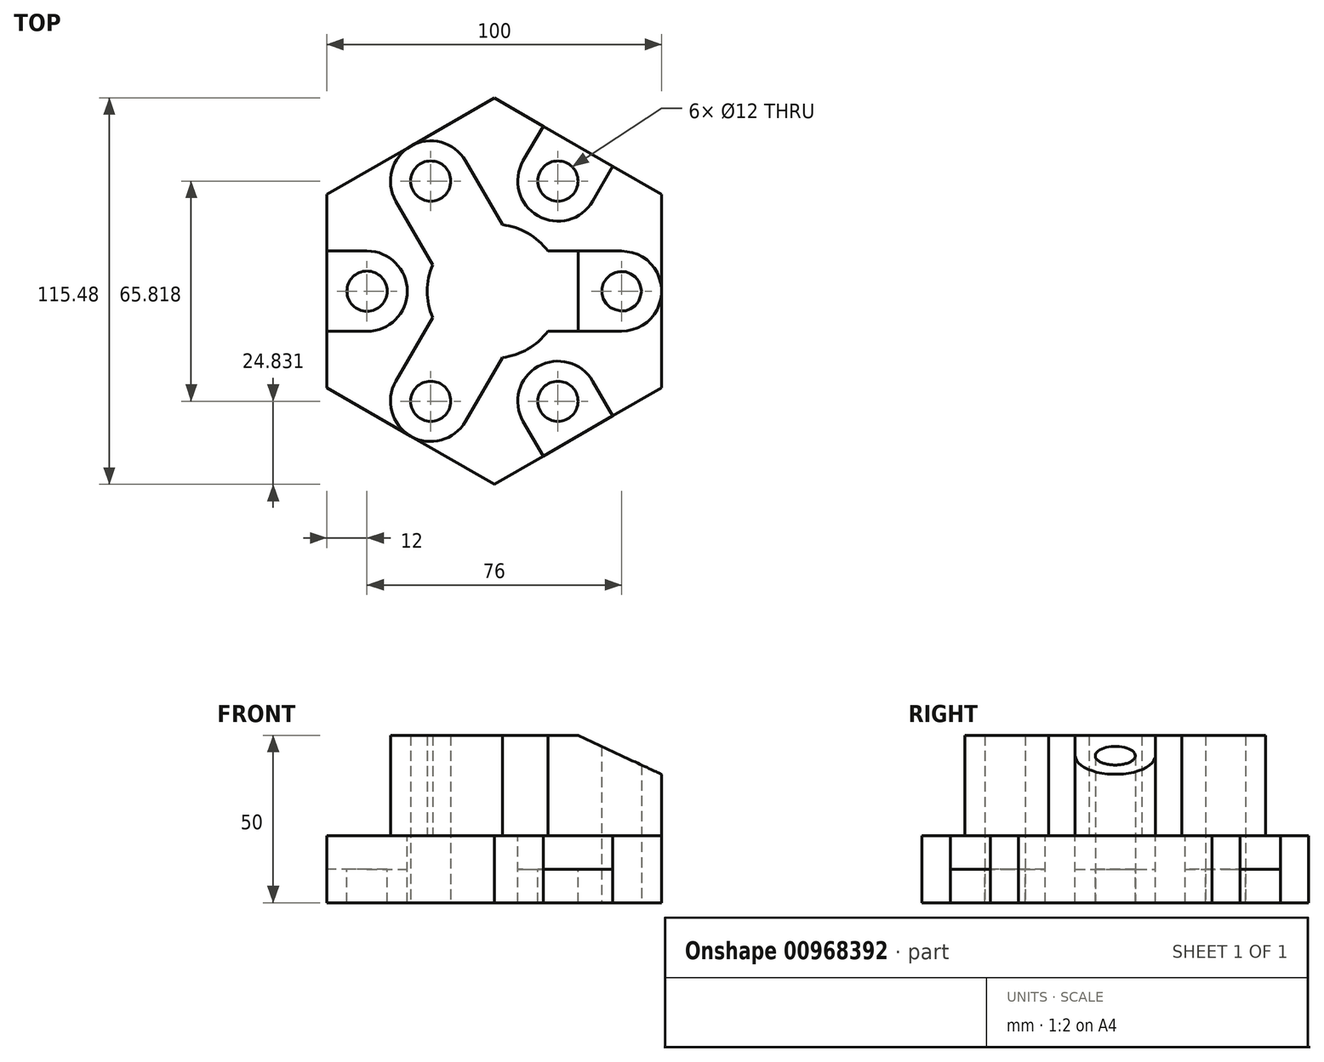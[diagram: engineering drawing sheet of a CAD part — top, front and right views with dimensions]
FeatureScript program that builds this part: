
annotation { "Feature Type Name" : "Feature", "Feature Type Description" : "" }
export const myFeature = defineFeature(function(context is Context, id is Id, definition is map)
    precondition{}
    {
        {
            var Q0;
            Q0=qCreatedBy(makeId("Top.planeOp"),FACE);
            cPlane(context, id + "F0", {"entities" : qUnion([Q0]), "cplaneType" : CPlaneType.OFFSET, "offset" : 20 * mm, "width" : 150 * mm, "height" : 150 * mm});
        }
        {
            var Q0;
            Q0=qCreatedBy(id+"F0.planeOp",FACE);
            var sketch = newSketch(context, id + "F1", { "sketchPlane" : qUnion([Q0])});
            skCircle(sketch, "E0.cCircle", {"center": v(0, 0) * mm, "radius": 50 * mm, "construction": true});
            skLineSegment(sketch, "E0.0", {"start": v(50, 28.87) * mm, "end": v(50, -28.87) * mm});
            skLineSegment(sketch, "E0.1", {"start": v(50, -28.87) * mm, "end": v(0, -57.74) * mm});
            skLineSegment(sketch, "E0.2", {"start": v(0, -57.74) * mm, "end": v(-50, -28.87) * mm});
            skLineSegment(sketch, "E0.3", {"start": v(-50, -28.87) * mm, "end": v(-50, 28.87) * mm});
            skLineSegment(sketch, "E0.4", {"start": v(-50, 28.87) * mm, "end": v(0, 57.74) * mm});
            skLineSegment(sketch, "E0.5", {"start": v(0, 57.74) * mm, "end": v(50, 28.87) * mm});
            skPoint(sketch, "E0.0.midPoint", {"position": v(50, 0) * mm});
            skLineSegment(sketch, "E1", {"start": v(-25, 43.3) * mm, "end": v(0, 0) * mm, "construction": true});
            skLineSegment(sketch, "E2", {"start": v(0, 0) * mm, "end": v(-25, -43.3) * mm, "construction": true});
            skArc(sketch, "E3", {"start": v(-18.4, 7.86) * mm, "mid": v(-20, 0) * mm, "end": v(-18.4, -7.86) * mm});
            skCircle(sketch, "E4", {"center": v(-19, 32.9) * mm, "radius": 6 * mm});
            skCircle(sketch, "E5", {"center": v(-19, -32.9) * mm, "radius": 6 * mm});
            skCircle(sketch, "E6", {"center": v(38, 0) * mm, "radius": 6 * mm});
            skCircle(sketch, "E7", {"center": v(0, 0) * mm, "radius": 38 * mm, "construction": true});
            skArc(sketch, "E8", {"start": v(-8.6, 38.9) * mm, "mid": v(-25, 43.3) * mm, "end": v(-29.4, 26.9) * mm});
            skArc(sketch, "E9", {"start": v(38, -12) * mm, "mid": v(50, 0) * mm, "end": v(38, 12) * mm});
            skArc(sketch, "E10", {"start": v(-29.4, -26.9) * mm, "mid": v(-25, -43.3) * mm, "end": v(-8.6, -38.9) * mm});
            skLineSegment(sketch, "E11", {"start": v(-29.4, 26.9) * mm, "end": v(-18.4, 7.86) * mm});
            skLineSegment(sketch, "E12", {"start": v(-8.6, 38.9) * mm, "end": v(2.4, 19.86) * mm});
            skLineSegment(sketch, "E13", {"start": v(-29.4, -26.9) * mm, "end": v(-18.4, -7.86) * mm});
            skLineSegment(sketch, "E14", {"start": v(-8.6, -38.9) * mm, "end": v(2.4, -19.86) * mm});
            skLineSegment(sketch, "E15", {"start": v(38, 12) * mm, "end": v(16, 12) * mm});
            skLineSegment(sketch, "E16", {"start": v(38, -12) * mm, "end": v(16, -12) * mm});
            skPoint(sketch, "E17.orphan", {"position": v(0, 24) * mm});
            skArc(sketch, "E18.trimOffspring", {"start": v(16, 12) * mm, "mid": v(10, 17.32) * mm, "end": v(2.4, 19.86) * mm});
            skArc(sketch, "E19.trimOffspring", {"start": v(2.4, -19.86) * mm, "mid": v(10, -17.32) * mm, "end": v(16, -12) * mm});
            skLineSegment(sketch, "E20", {"start": v(-22.9, 15.65) * mm, "end": v(-2.1, 27.65) * mm});
            skLineSegment(sketch, "E21", {"start": v(25, 12) * mm, "end": v(25, -12) * mm});
            skLineSegment(sketch, "E22", {"start": v(-22.9, -15.65) * mm, "end": v(-2.1, -27.65) * mm});
            skLineSegment(sketch, "E23", {"start": v(0, 0) * mm, "end": v(25, 43.3) * mm, "construction": true});
            skLineSegment(sketch, "E24", {"start": v(0, 0) * mm, "end": v(25, -43.3) * mm, "construction": true});
            skLineSegment(sketch, "E25", {"start": v(-50, 0) * mm, "end": v(0, 0) * mm, "construction": true});
            skCircle(sketch, "E26", {"center": v(19, 32.9) * mm, "radius": 6 * mm});
            skCircle(sketch, "E27", {"center": v(19, -32.9) * mm, "radius": 6 * mm});
            skCircle(sketch, "E28", {"center": v(-38, 0) * mm, "radius": 6 * mm});
            skArc(sketch, "E29", {"start": v(29.4, -26.9) * mm, "mid": v(13, -22.52) * mm, "end": v(8.6, -38.9) * mm});
            skArc(sketch, "E30", {"start": v(8.6, 38.9) * mm, "mid": v(13, 22.52) * mm, "end": v(29.4, 26.9) * mm});
            skArc(sketch, "E31", {"start": v(-38, -12) * mm, "mid": v(-26, 0) * mm, "end": v(-38, 12) * mm});
            skLineSegment(sketch, "E32", {"start": v(8.6, 38.9) * mm, "end": v(14.6, 49.3) * mm});
            skLineSegment(sketch, "E33", {"start": v(29.4, 26.9) * mm, "end": v(35.4, 37.3) * mm});
            skLineSegment(sketch, "E34", {"start": v(8.6, -38.9) * mm, "end": v(14.6, -49.3) * mm});
            skLineSegment(sketch, "E35", {"start": v(29.4, -26.9) * mm, "end": v(35.4, -37.3) * mm});
            skLineSegment(sketch, "E36", {"start": v(-38, 12) * mm, "end": v(-50, 12) * mm});
            skLineSegment(sketch, "E37", {"start": v(-38, -12) * mm, "end": v(-50, -12) * mm});
            skLineSegment(sketch, "E38", {"start": v(-38, 12) * mm, "end": v(-38, -12) * mm, "construction": true});
            skSolve(sketch);
        }
        {
            var Q0;
            {var subQ9=sQuery(id+"F1.wireOp",EDGE,"E3");Q0=makeQuery(id+"F1.imprint","IMPRINT",FACE,{"disambiguationData":[TD([[makeQuery(id+"F1.imprint","IMPRINT",EDGE,{"derivedFrom":subQ9}),-1.0]])]});}
            var Q1;
            Q1=makeQuery(id+"F1.imprint","IMPRINT",FACE,{"disambiguationData":[TD([[makeQuery(id+"F1.imprint","IMPRINT",EDGE,{"derivedFrom":sQuery(id+"F1.wireOp",EDGE,"E28")}),-1.0]])]});
            var Q2;
            {var subQ0=sQuery(id+"F1.wireOp",EDGE,"E19.trimOffspring");Q2=makeQuery(id+"F1.imprint","IMPRINT",FACE,{"disambiguationData":[TD([[makeQuery(id+"F1.imprint","IMPRINT",EDGE,{"derivedFrom":subQ0}),-1.0]])]});}
            var Q3;
            Q3=makeQuery(id+"F1.imprint","IMPRINT",FACE,{"disambiguationData":[TD([[makeQuery(id+"F1.imprint","IMPRINT",EDGE,{"derivedFrom":sQuery(id+"F1.wireOp",EDGE,"E27")}),-1.0]])]});
            var Q4;
            {var subQ0=sQuery(id+"F1.wireOp",EDGE,"E18.trimOffspring");Q4=makeQuery(id+"F1.imprint","IMPRINT",FACE,{"disambiguationData":[TD([[makeQuery(id+"F1.imprint","IMPRINT",EDGE,{"derivedFrom":subQ0}),-1.0]])]});}
            var Q5;
            Q5=makeQuery(id+"F1.imprint","IMPRINT",FACE,{"disambiguationData":[TD([[makeQuery(id+"F1.imprint","IMPRINT",EDGE,{"derivedFrom":sQuery(id+"F1.wireOp",EDGE,"E26")}),-1.0]])]});
            var Q6;
            Q6=qCreatedBy(makeId("Top.planeOp"),FACE);
            extrude(context, id + "F2", {"entities" : qUnion([Q0, Q1, Q2, Q3, Q4, Q5]), "endBound" : BoundingType.UP_TO_SURFACE, "oppositeDirection" : true, "depth" : 20 * mm, "endBoundEntityFace" : qUnion([Q6]), "offsetDistance" : 25 * mm});
        }
        {
            var Q0;
            Q0=makeQuery(id+"F1.imprint","IMPRINT",FACE,{"disambiguationData":[TD([[makeQuery(id+"F1.imprint","IMPRINT",EDGE,{"derivedFrom":sQuery(id+"F1.wireOp",EDGE,"E4")}),-1.0]])]});
            var Q1;
            {var subQ1=sQuery(id+"F1.wireOp",EDGE,"E3");Q1=makeQuery(id+"F1.imprint","IMPRINT",FACE,{"disambiguationData":[TD([[makeQuery(id+"F1.imprint","IMPRINT",EDGE,{"derivedFrom":subQ1}),1.0]])]});}
            var Q2;
            Q2=makeQuery(id+"F1.imprint","IMPRINT",FACE,{"disambiguationData":[TD([[makeQuery(id+"F1.imprint","IMPRINT",EDGE,{"derivedFrom":sQuery(id+"F1.wireOp",EDGE,"E6")}),-1.0]])]});
            var Q3;
            Q3=makeQuery(id+"F1.imprint","IMPRINT",FACE,{"disambiguationData":[TD([[makeQuery(id+"F1.imprint","IMPRINT",EDGE,{"derivedFrom":sQuery(id+"F1.wireOp",EDGE,"E5")}),-1.0]])]});
            var Q4;
            Q4=qCreatedBy(makeId("Top.planeOp"),FACE);
            extrude(context, id + "F3", {"entities" : qUnion([Q0, Q1, Q2, Q3]), "operationType" : NewBodyOperationType.ADD, "depth" : 30 * mm, "offsetDistance" : 25 * mm, "hasSecondDirection" : true, "secondDirectionBound" : BoundingType.UP_TO_SURFACE, "secondDirectionOppositeDirection" : true, "secondDirectionDepth" : 25 * mm, "secondDirectionBoundEntityFace" : qUnion([Q4])});
        }
        {
            var Q0;
            Q0=makeQuery(id+"F1.imprint","IMPRINT",FACE,{"disambiguationData":[TD([[makeQuery(id+"F1.imprint","IMPRINT",EDGE,{"derivedFrom":sQuery(id+"F1.wireOp",EDGE,"E28")}),-1.0]])]});
            var Q1;
            Q1=makeQuery(id+"F1.imprint","IMPRINT",FACE,{"disambiguationData":[TD([[makeQuery(id+"F1.imprint","IMPRINT",EDGE,{"derivedFrom":sQuery(id+"F1.wireOp",EDGE,"E27")}),-1.0]])]});
            var Q2;
            Q2=makeQuery(id+"F1.imprint","IMPRINT",FACE,{"disambiguationData":[TD([[makeQuery(id+"F1.imprint","IMPRINT",EDGE,{"derivedFrom":sQuery(id+"F1.wireOp",EDGE,"E26")}),-1.0]])]});
            extrude(context, id + "F4", {"entities" : qUnion([Q0, Q1, Q2]), "operationType" : NewBodyOperationType.REMOVE, "oppositeDirection" : true, "depth" : 10 * mm, "offsetDistance" : 25 * mm});
        }
        {
            var Q0;
            Q0=qCreatedBy(makeId("Front.planeOp"),FACE);
            var sketch = newSketch(context, id + "F5", { "sketchPlane" : qUnion([Q0])});
            skLineSegment(sketch, "E39", {"start": v(32, 20) * mm, "end": v(25, 20) * mm});
            skLineSegment(sketch, "E40", {"start": v(50, 20) * mm, "end": v(44, 20) * mm});
            skLineSegment(sketch, "E41", {"start": v(25, 50) * mm, "end": v(50, 38.34) * mm});
            skLineSegment(sketch, "E42", {"start": v(25, 50) * mm, "end": v(25, 20) * mm, "construction": true});
            skLineSegment(sketch, "E43", {"start": v(50, 20) * mm, "end": v(50, 38.34) * mm});
            skLineSegment(sketch, "E44", {"start": v(25, 50) * mm, "end": v(50, 50) * mm});
            skLineSegment(sketch, "E45", {"start": v(50, 50) * mm, "end": v(50, 38.34) * mm});
            skSolve(sketch);
        }
        {
            var Q0;
            Q0=makeQuery(id+"F5.imprint","IMPRINT",FACE,{"disambiguationData":[TD([[makeQuery(id+"F5.imprint","IMPRINT",EDGE,{"derivedFrom":sQuery(id+"F5.wireOp",EDGE,"E41")}),1.0]])]});
            extrude(context, id + "F6", {"entities" : qUnion([Q0]), "operationType" : NewBodyOperationType.REMOVE, "depth" : 25 * mm, "offsetDistance" : 25 * mm, "symmetric" : true});
        }
    });
